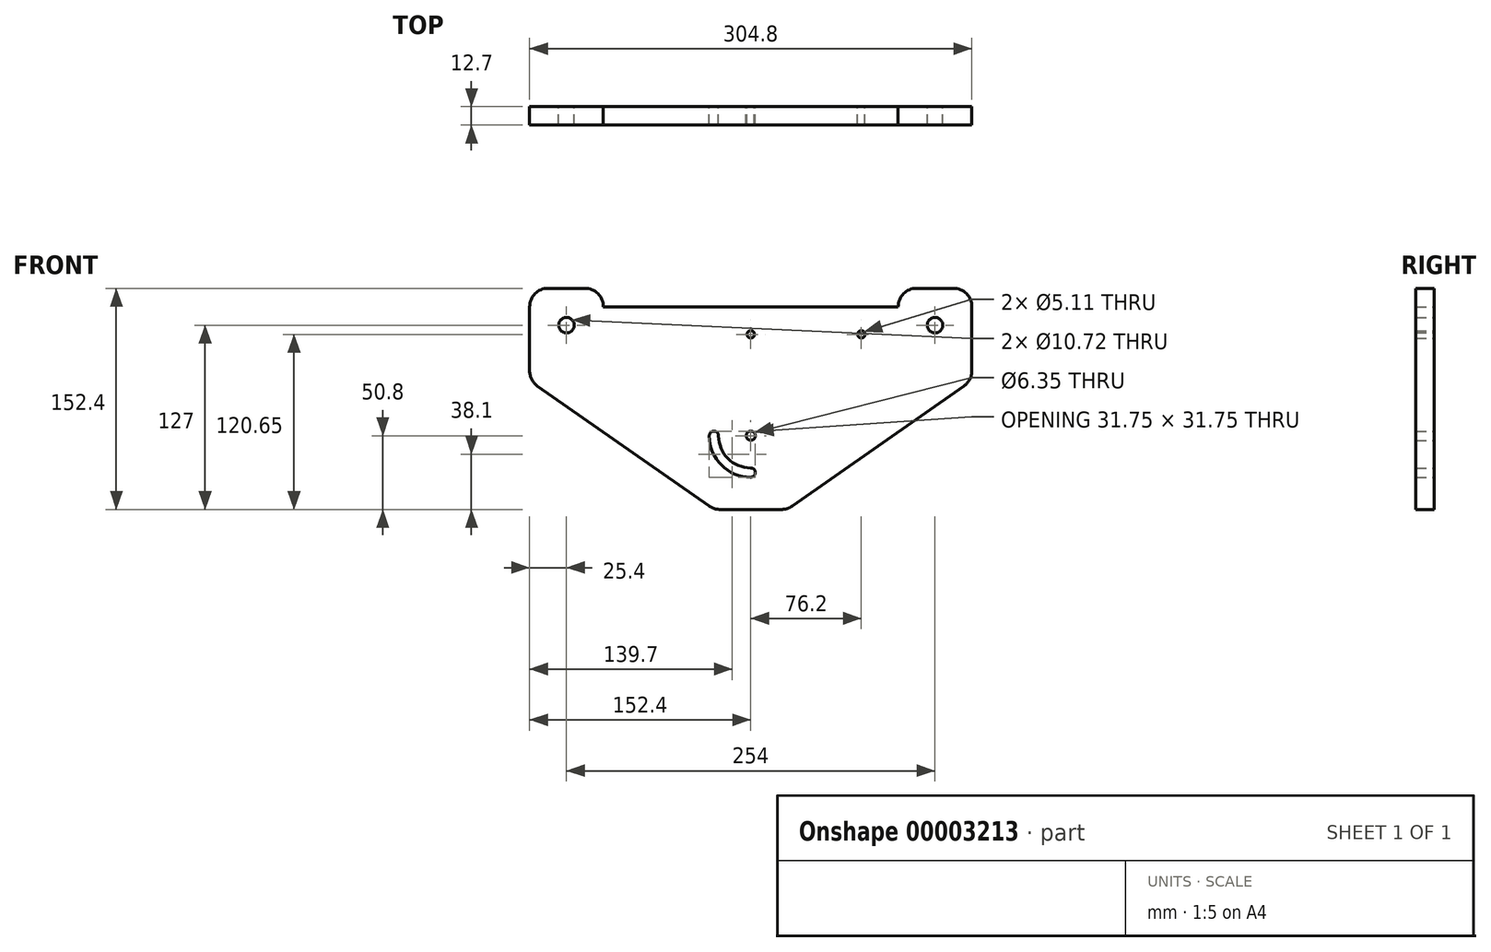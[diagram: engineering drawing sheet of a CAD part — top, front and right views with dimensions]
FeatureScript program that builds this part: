
annotation { "Feature Type Name" : "Feature", "Feature Type Description" : "" }
export const myFeature = defineFeature(function(context is Context, id is Id, definition is map)
    precondition{}
    {
        {
            var Q0;
            Q0=qCreatedBy(makeId("Front.planeOp"),FACE);
            var sketch = newSketch(context, id + "F0", { "sketchPlane" : qUnion([Q0])});
            skLineSegment(sketch, "E0", {"start": v(0, 0) * mm, "end": v(0, -101.6) * mm});
            skLineSegment(sketch, "E1", {"start": v(127, -152.4) * mm, "end": v(177.8, -152.4) * mm});
            skLineSegment(sketch, "E2", {"start": v(304.8, 0) * mm, "end": v(254, 0) * mm});
            skLineSegment(sketch, "E3", {"start": v(152.4, -12.7) * mm, "end": v(152.4, -152.4) * mm, "construction": true});
            skLineSegment(sketch, "E4", {"start": v(127, -12.7) * mm, "end": v(127, -152.4) * mm, "construction": true});
            skLineSegment(sketch, "E5", {"start": v(177.8, -12.7) * mm, "end": v(177.8, -152.4) * mm, "construction": true});
            skLineSegment(sketch, "E6", {"start": v(25.4, -101.6) * mm, "end": v(304.8, -101.6) * mm, "construction": true});
            skCircle(sketch, "E7", {"center": v(152.4, -101.6) * mm, "radius": 3.18 * mm});
            skArc(sketch, "E8", {"start": v(130.18, -101.6) * mm, "mid": v(127, -98.42) * mm, "end": v(123.83, -101.6) * mm});
            skArc(sketch, "E9", {"start": v(123.82, -101.6) * mm, "mid": v(132.2, -121.8) * mm, "end": v(152.4, -130.17) * mm});
            skArc(sketch, "E10", {"start": v(130.18, -101.6) * mm, "mid": v(136.68, -117.32) * mm, "end": v(152.4, -123.82) * mm});
            skPoint(sketch, "E11.center.orphan", {"position": v(152.4, -127) * mm});
            skLineSegment(sketch, "E12", {"start": v(50.8, 0) * mm, "end": v(50.8, -152.4) * mm, "construction": true});
            skLineSegment(sketch, "E13", {"start": v(254, 0) * mm, "end": v(254, -152.4) * mm, "construction": true});
            skLineSegment(sketch, "E14", {"start": v(0, -63.5) * mm, "end": v(304.8, -63.5) * mm, "construction": true});
            skLineSegment(sketch, "E15", {"start": v(0, -25.4) * mm, "end": v(304.8, -25.4) * mm, "construction": true});
            skLineSegment(sketch, "E16", {"start": v(0, -12.7) * mm, "end": v(304.8, -12.7) * mm, "construction": true});
            skLineSegment(sketch, "E17", {"start": v(50.8, 0) * mm, "end": v(50.8, -12.7) * mm});
            skLineSegment(sketch, "E18", {"start": v(50.8, -12.7) * mm, "end": v(254, -12.7) * mm});
            skLineSegment(sketch, "E19", {"start": v(254, -12.7) * mm, "end": v(254, 0) * mm});
            skLineSegment(sketch, "E20", {"start": v(0, -31.75) * mm, "end": v(304.8, -31.75) * mm, "construction": true});
            skCircle(sketch, "E21", {"center": v(152.4, -31.75) * mm, "radius": 2.55 * mm});
            skLineSegment(sketch, "E22", {"start": v(25.4, 0) * mm, "end": v(25.4, -81.28) * mm, "construction": true});
            skLineSegment(sketch, "E23", {"start": v(279.4, 0) * mm, "end": v(279.4, -152.4) * mm, "construction": true});
            skCircle(sketch, "E24", {"center": v(279.4, -25.4) * mm, "radius": 5.36 * mm});
            skCircle(sketch, "E25", {"center": v(25.4, -25.4) * mm, "radius": 5.36 * mm});
            skLineSegment(sketch, "E26", {"start": v(228.6, -12.7) * mm, "end": v(228.6, -152.4) * mm, "construction": true});
            skCircle(sketch, "E27", {"center": v(228.6, -31.75) * mm, "radius": 2.55 * mm});
            skLineSegment(sketch, "E28.trimOffspring", {"start": v(50.8, 0) * mm, "end": v(0, 0) * mm});
            skPoint(sketch, "E29.orphan", {"position": v(152.4, 0) * mm});
            skLineSegment(sketch, "E30", {"start": v(0, -63.5) * mm, "end": v(127, -152.4) * mm});
            skLineSegment(sketch, "E31", {"start": v(177.8, -152.4) * mm, "end": v(304.8, -63.5) * mm});
            skLineSegment(sketch, "E32.trimOffspring", {"start": v(304.8, -63.5) * mm, "end": v(304.8, 0) * mm});
            skPoint(sketch, "E33.trimOffspring.end.orphan", {"position": v(0, -152.4) * mm});
            skLineSegment(sketch, "E34.trimOffspring", {"start": v(50.8, -127) * mm, "end": v(304.8, -127) * mm, "construction": true});
            skPoint(sketch, "E35.start.orphan", {"position": v(0, -127) * mm});
            skPoint(sketch, "E36.orphan", {"position": v(304.8, -152.4) * mm});
            skArc(sketch, "E37", {"start": v(152.4, -130.17) * mm, "mid": v(155.58, -127) * mm, "end": v(152.4, -123.82) * mm});
            skSolve(sketch);
        }
        {
            var Q0;
            Q0 = qSketchRegion(id + "F0", true);
            extrude(context, id + "F1", {"entities" : qUnion([Q0]), "endBound" : BoundingType.SYMMETRIC, "depth" : 12.7 * mm});
        }
        {
            var Q0;
            Q0=makeQuery(id+"F1.opExtrude","SWEPT_EDGE",EDGE,{"disambiguationData":[OSD([sQuery(id+"F0.wireOp",EDGE,"E2"),sQuery(id+"F0.wireOp",EDGE,"E32.trimOffspring")])]});
            var Q1;
            Q1=makeQuery(id+"F1.opExtrude","SWEPT_EDGE",EDGE,{"disambiguationData":[OSD([sQuery(id+"F0.wireOp",EDGE,"E0"),sQuery(id+"F0.wireOp",EDGE,"E28.trimOffspring")])]});
            var Q2;
            Q2=makeQuery(id+"F1.opExtrude","SWEPT_EDGE",EDGE,{"disambiguationData":[OSD([sQuery(id+"F0.wireOp",EDGE,"E0"),sQuery(id+"F0.wireOp",EDGE,"E30")])]});
            var Q3;
            Q3=makeQuery(id+"F1.opExtrude","SWEPT_EDGE",EDGE,{"disambiguationData":[OSD([sQuery(id+"F0.wireOp",EDGE,"E31"),sQuery(id+"F0.wireOp",EDGE,"E32.trimOffspring")])]});
            var Q4;
            Q4=makeQuery(id+"F1.opExtrude","SWEPT_EDGE",EDGE,{"disambiguationData":[OSD([sQuery(id+"F0.wireOp",EDGE,"E1"),sQuery(id+"F0.wireOp",EDGE,"E31")])]});
            var Q5;
            Q5=makeQuery(id+"F1.opExtrude","SWEPT_EDGE",EDGE,{"disambiguationData":[OSD([sQuery(id+"F0.wireOp",EDGE,"E1"),sQuery(id+"F0.wireOp",EDGE,"E30")])]});
            fillet(context, id + "F2", {"entities" : qUnion([Q0, Q1, Q2, Q3, Q4, Q5]), "radius" : 12.7 * mm, "tangentPropagation" : true, "allowEdgeOverflow" : false});
        }
        {
            var Q0;
            Q0=makeQuery(id+"F1.opExtrude","SWEPT_EDGE",EDGE,{"disambiguationData":[OSD([sQuery(id+"F0.wireOp",EDGE,"E2"),sQuery(id+"F0.wireOp",EDGE,"E19")])]});
            var Q1;
            Q1=makeQuery(id+"F1.opExtrude","SWEPT_EDGE",EDGE,{"disambiguationData":[OSD([sQuery(id+"F0.wireOp",EDGE,"E17"),sQuery(id+"F0.wireOp",EDGE,"E28.trimOffspring")])]});
            fillet(context, id + "F3", {"entities" : qUnion([Q0, Q1]), "radius" : 12.7 * mm, "tangentPropagation" : true, "allowEdgeOverflow" : false});
        }
    });
